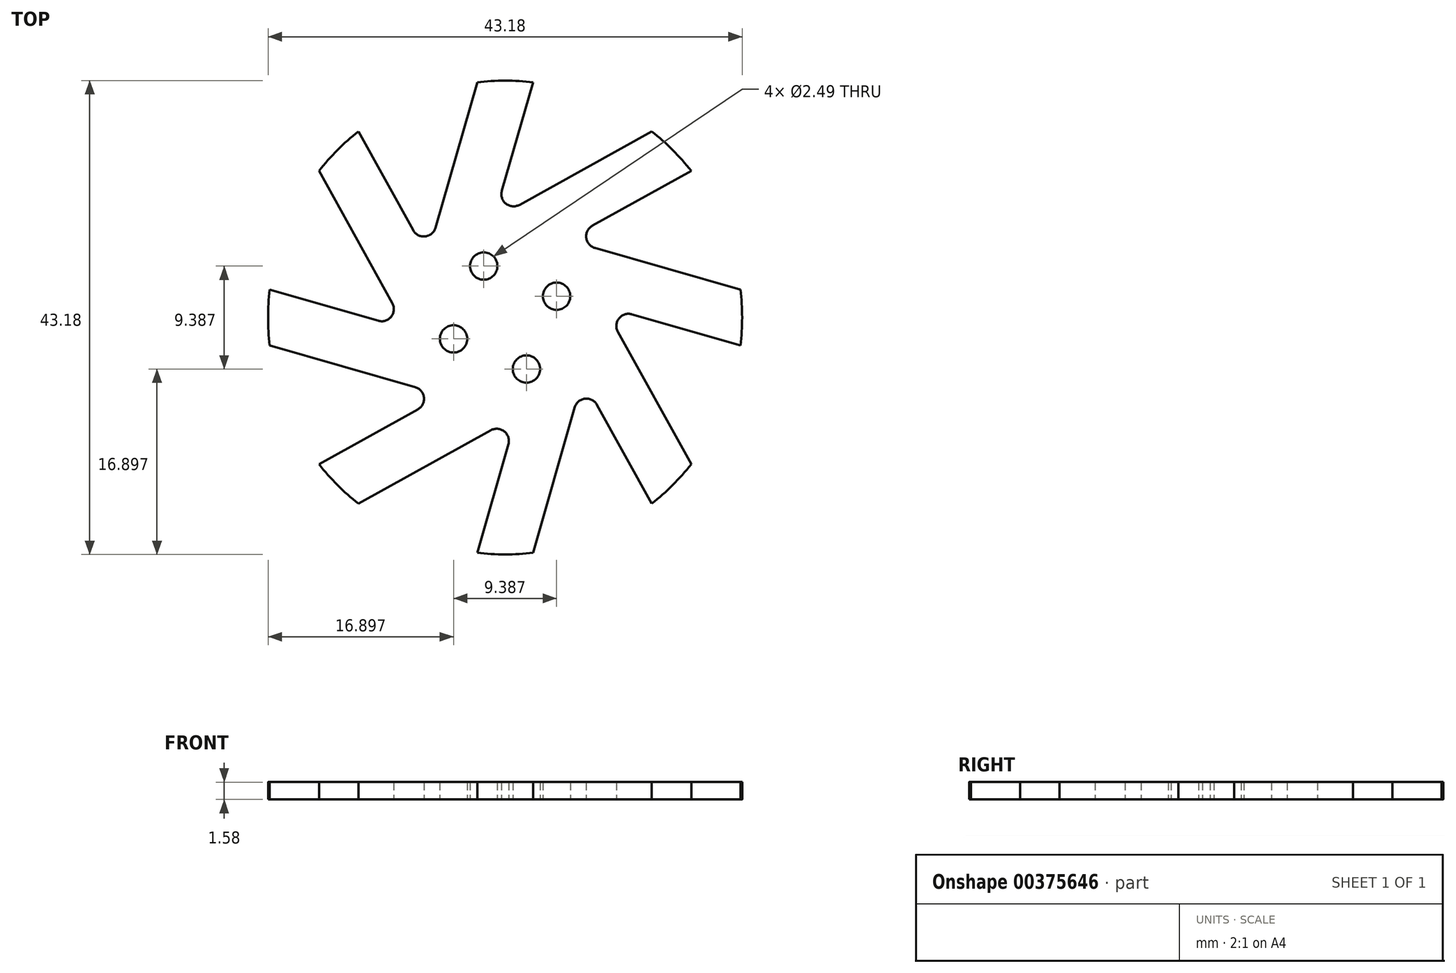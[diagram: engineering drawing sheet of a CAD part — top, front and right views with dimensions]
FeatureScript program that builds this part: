
annotation { "Feature Type Name" : "Feature", "Feature Type Description" : "" }
export const myFeature = defineFeature(function(context is Context, id is Id, definition is map)
    precondition{}
    {
        {
            var Q0;
            Q0=qCreatedBy(makeId("Top.planeOp"),FACE);
            var sketch = newSketch(context, id + "F0", { "sketchPlane" : qUnion([Q0])});
            skLineSegment(sketch, "E0", {"start": v(0, 30.67) * mm, "end": v(0, -28.01) * mm, "construction": true});
            skLineSegment(sketch, "E1", {"start": v(-28.25, 0) * mm, "end": v(29.1, 0) * mm, "construction": true});
            skLineSegment(sketch, "E2", {"start": v(-21.4, 21.4) * mm, "end": v(20.62, -20.62) * mm, "construction": true});
            skLineSegment(sketch, "E3", {"start": v(21.66, 21.66) * mm, "end": v(-18.96, -18.96) * mm, "construction": true});
            skArc(sketch, "E4", {"start": v(-16.96, 13.36) * mm, "mid": v(-15.27, 15.27) * mm, "end": v(-13.36, 16.96) * mm});
            skArc(sketch, "E5", {"start": v(-2.54, 21.44) * mm, "mid": v(0, 21.59) * mm, "end": v(2.54, 21.44) * mm});
            skArc(sketch, "E6", {"start": v(13.36, 16.96) * mm, "mid": v(15.27, 15.27) * mm, "end": v(16.96, 13.36) * mm});
            skArc(sketch, "E7", {"start": v(21.44, 2.54) * mm, "mid": v(21.6, 0) * mm, "end": v(21.44, -2.54) * mm});
            skArc(sketch, "E8", {"start": v(16.96, -13.36) * mm, "mid": v(15.27, -15.27) * mm, "end": v(13.36, -16.96) * mm});
            skArc(sketch, "E9", {"start": v(2.54, -21.44) * mm, "mid": v(0, -21.6) * mm, "end": v(-2.54, -21.44) * mm});
            skArc(sketch, "E10", {"start": v(-13.36, -16.96) * mm, "mid": v(-15.27, -15.27) * mm, "end": v(-16.96, -13.36) * mm});
            skArc(sketch, "E11", {"start": v(-21.44, -2.54) * mm, "mid": v(-21.59, 0) * mm, "end": v(-21.44, 2.54) * mm});
            skCircle(sketch, "E12", {"center": v(0, 0) * mm, "radius": 5.08 * mm, "construction": true});
            skCircle(sketch, "E13", {"center": v(4.7, 1.94) * mm, "radius": 1.24 * mm});
            skCircle(sketch, "E14", {"center": v(-4.7, -1.94) * mm, "radius": 1.24 * mm});
            skCircle(sketch, "E15", {"center": v(1.94, -4.7) * mm, "radius": 1.24 * mm});
            skLineSegment(sketch, "E16", {"start": v(-2.42, 5.85) * mm, "end": v(2.68, -6.46) * mm, "construction": true});
            skLineSegment(sketch, "E17", {"start": v(6.63, 2.74) * mm, "end": v(-6.69, -2.77) * mm, "construction": true});
            skCircle(sketch, "E18", {"center": v(-1.94, 4.7) * mm, "radius": 1.24 * mm});
            skCircle(sketch, "E19", {"center": v(0, 0) * mm, "radius": 10.16 * mm, "construction": true});
            skLineSegment(sketch, "E20", {"start": v(13.36, 16.96) * mm, "end": v(1.3, 10.27) * mm});
            skLineSegment(sketch, "E21", {"start": v(16.96, 13.36) * mm, "end": v(7.96, 8.38) * mm});
            skLineSegment(sketch, "E22", {"start": v(2.54, 21.44) * mm, "end": v(-0.3, 11.55) * mm});
            skLineSegment(sketch, "E23", {"start": v(-2.54, 21.44) * mm, "end": v(-6.34, 8.19) * mm});
            skLineSegment(sketch, "E24", {"start": v(-13.36, 16.96) * mm, "end": v(-8.38, 7.96) * mm});
            skLineSegment(sketch, "E25", {"start": v(-16.96, 13.36) * mm, "end": v(-10.27, 1.3) * mm});
            skLineSegment(sketch, "E26", {"start": v(-21.44, 2.54) * mm, "end": v(-11.55, -0.3) * mm});
            skLineSegment(sketch, "E27", {"start": v(-21.44, -2.54) * mm, "end": v(-8.19, -6.34) * mm});
            skLineSegment(sketch, "E28", {"start": v(-16.96, -13.36) * mm, "end": v(-7.96, -8.38) * mm});
            skLineSegment(sketch, "E29", {"start": v(-13.36, -16.96) * mm, "end": v(-1.3, -10.27) * mm});
            skLineSegment(sketch, "E30", {"start": v(-2.54, -21.44) * mm, "end": v(0.3, -11.55) * mm});
            skLineSegment(sketch, "E31", {"start": v(2.54, -21.44) * mm, "end": v(6.34, -8.19) * mm});
            skLineSegment(sketch, "E32", {"start": v(13.36, -16.96) * mm, "end": v(8.38, -7.96) * mm});
            skLineSegment(sketch, "E33", {"start": v(16.96, -13.36) * mm, "end": v(10.27, -1.3) * mm});
            skLineSegment(sketch, "E34", {"start": v(21.44, -2.54) * mm, "end": v(11.55, 0.3) * mm});
            skLineSegment(sketch, "E35", {"start": v(21.44, 2.54) * mm, "end": v(8.19, 6.34) * mm});
            skArc(sketch, "E36", {"start": v(-0.3, 11.55) * mm, "mid": v(0.08, 10.37) * mm, "end": v(1.3, 10.27) * mm});
            skArc(sketch, "E37", {"start": v(-8.38, 7.96) * mm, "mid": v(-7.28, 7.4) * mm, "end": v(-6.34, 8.19) * mm});
            skArc(sketch, "E38", {"start": v(-11.55, -0.3) * mm, "mid": v(-10.37, 0.08) * mm, "end": v(-10.27, 1.3) * mm});
            skArc(sketch, "E39", {"start": v(-7.96, -8.38) * mm, "mid": v(-7.4, -7.28) * mm, "end": v(-8.19, -6.34) * mm});
            skArc(sketch, "E40", {"start": v(0.3, -11.55) * mm, "mid": v(-0.08, -10.37) * mm, "end": v(-1.3, -10.27) * mm});
            skArc(sketch, "E41", {"start": v(8.38, -7.96) * mm, "mid": v(7.28, -7.4) * mm, "end": v(6.34, -8.19) * mm});
            skArc(sketch, "E42", {"start": v(11.55, 0.3) * mm, "mid": v(10.37, -0.08) * mm, "end": v(10.27, -1.3) * mm});
            skArc(sketch, "E43", {"start": v(7.96, 8.38) * mm, "mid": v(7.4, 7.28) * mm, "end": v(8.19, 6.34) * mm});
            skSolve(sketch);
        }
        {
            var Q0;
            Q0=qSketchRegion(id+"F0",true);
            extrude(context, id + "F1", {"entities" : qUnion([Q0]), "endBound" : BoundingType.SYMMETRIC, "depth" : 1.59 * mm});
        }
        {
            var Q0;
            Q0=qCreatedBy(makeId("Front.planeOp"),FACE);
            var sketch = newSketch(context, id + "F2", { "sketchPlane" : qUnion([Q0])});
            skLineSegment(sketch, "E44", {"start": v(0, 9.03) * mm, "end": v(0, -9.77) * mm, "construction": true});
            skSolve(sketch);
        }
        {
            var Q0;
            Q0=makeQuery(id+"F1.opExtrude","CAP_EDGE",EDGE,{"disambiguationData":[OSD([sQuery(id+"F0.wireOp",EDGE,"E6")])],"isStart":false});
            cPoint(context, id + "F3", {"entities" : qUnion([Q0]), "parameter" : 0.5});
        }
        {
            var Q0;
            Q0=makeQuery(id+"F1.opExtrude","CAP_EDGE",EDGE,{"disambiguationData":[OSD([sQuery(id+"F0.wireOp",EDGE,"E6")])],"isStart":false});
            var Q1;
            Q1=qCreatedBy(id+"F3",VERTEX);
            cPlane(context, id + "F4", {"entities" : qUnion([Q0, Q1]), "cplaneType" : CPlaneType.CURVE_POINT, "offset" : 25.4 * mm, "width" : 152.4 * mm, "height" : 152.4 * mm});
        }
    });
